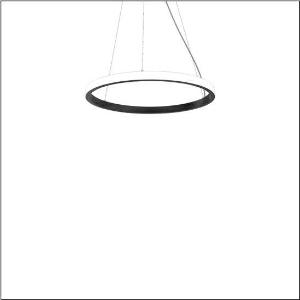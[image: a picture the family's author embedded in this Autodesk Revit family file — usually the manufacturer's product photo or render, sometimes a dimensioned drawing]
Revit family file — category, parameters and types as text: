
# Revit family: silica_r__21_ring-o_5pjbo2d3104a_e544
name_source: partatom
category: Lighting Fixtures
units: mm (PartAtom-declared; Revit-internal decimal feet)

## family parameters
Cut with Voids When Loaded = No
Host = Face
Light Source = No
Part Type = Normal
Room Calculation Point = No
Round Connector Dimension = Use Diameter
Shared = No

## types (1)
- Silica® 21 Ring-O (1 x LED, 4940 lm, 80 W, 4000K)
    Apparent Load = 80 VA
    CIE Flux Codes = 2 16 49 50 100
    Color Rendering = 80
    Color Temperature = 4000K
    Default Elevation = 1800 mm
    Description = Silica® 21 Ring-O, suspended luminaire, of PMMA, frosted, light emission: outer ring side luminous distribution, primary light characteristic: symmetric, installation type: suspended mounting, LED, rated luminous flux: 4.940lm, luminous efficacy: 62lm/W, light colour: 840, colour temperature: 4000K, control gear: DALI 2, with terminal, 5-pole, mains connection: 230V, AC/DC, 0/50..60Hz, rated input power: 80W, housing, of extruded aluminium section, jet black (RAL 9005), diameter: 810mm, ceiling canopy, jet black (RAL 9005), protection rating (lamp compartment): IP40, insulation class (complete): insulation class I (protective earthing), certification: CE, impact resistance: IK02, permissible operating ambient temperature: 0..+35°C, packaging unit: 1 piece
    Height = 48 mm  [stored 0.15748 ft]
    Lamp = 1 x LED
    Lamp Light Flux = 4940 lm
    Lamp Power = 80 W
    Lamp count = 1
    Length = 810 mm
    Luminous efficacy = 62 lm/W
    Manufacturer = Siteco
    ModVariant = No
    Model = 5PJBO2D3104A
    Mounting Place = Ceiling
    Mounting Type = Pendant
    Number of Poles = 1
    OnlyDefault = Yes
    Power Factor = 1
    Product Name = Silica® 21 Ring-O
    Product group = suspended luminaire
    ProductGroupID = 905
    Protection Class = Protection class I
    Protection Degree = IP 40
    RLX_Detail_Level = 1
    RLX_Emergency_Light_Flux = 0 lm
    RLX_Emergency_Type = 0
    RLX_Emergency_Type_DB = No
    RlxData = <blob elided: 14089 chars, md5=452c772e>
    Socket = socket
    Standby Power = 0 W
    System Light Flux = 4940 lm
    System Power = 80 W
    Type Comments = Product without accessories
    Type Image = l_1258381.jpg
    URL = http://relux.com
    VarID = ---
    Voltage = 0 V
    Weight = 0.00 kg
    Width = 0 mm  [stored 0 ft]

note: [stored X ft] marks values corroborated as IEEE doubles in the binary element streams (Revit-internal decimal feet)

## geometry (parser evidence)
native form markers: Sweep x14
no freeform markers — native parametric forms only
